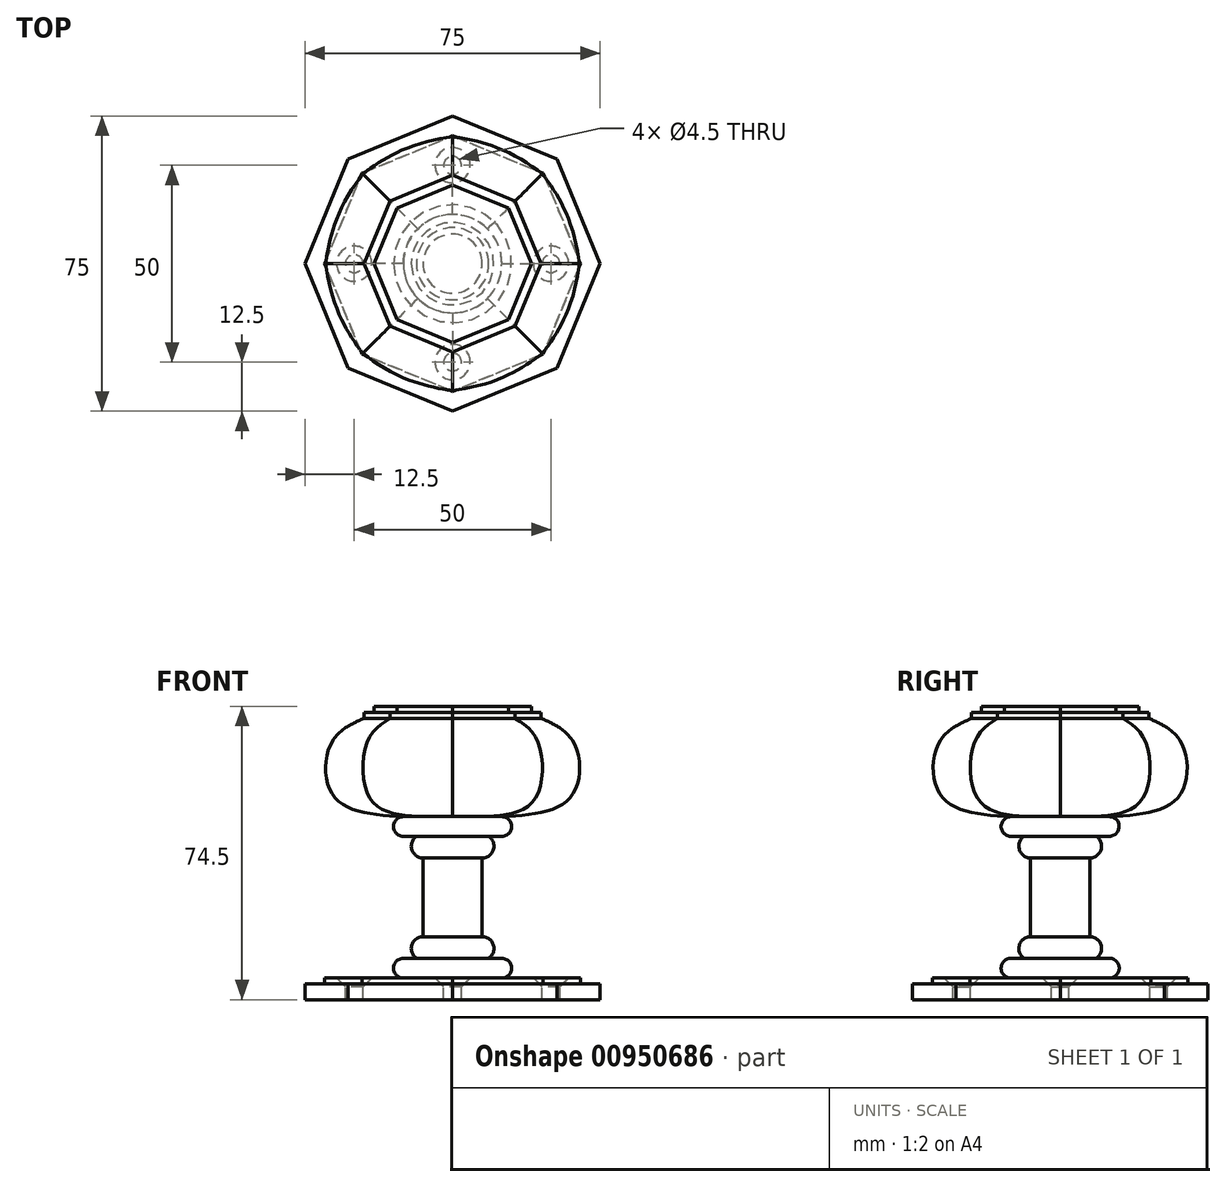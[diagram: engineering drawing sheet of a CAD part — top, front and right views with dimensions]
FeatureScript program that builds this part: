
annotation { "Feature Type Name" : "Feature", "Feature Type Description" : "" }
export const myFeature = defineFeature(function(context is Context, id is Id, definition is map)
    precondition{}
    {
        {
            var Q0;
            Q0=qCreatedBy(makeId("Top.planeOp"),FACE);
            var sketch = newSketch(context, id + "F0", { "sketchPlane" : qUnion([Q0])});
            skCircle(sketch, "E0.cCircle", {"center": v(0, 0) * mm, "radius": 37.5 * mm, "construction": true});
            skLineSegment(sketch, "E0.0", {"start": v(37.5, 0) * mm, "end": v(26.52, -26.52) * mm});
            skLineSegment(sketch, "E0.1", {"start": v(26.52, -26.52) * mm, "end": v(0, -37.5) * mm});
            skLineSegment(sketch, "E0.2", {"start": v(0, -37.5) * mm, "end": v(-26.52, -26.52) * mm});
            skLineSegment(sketch, "E0.3", {"start": v(-26.52, -26.52) * mm, "end": v(-37.5, 0) * mm});
            skLineSegment(sketch, "E0.4", {"start": v(-37.5, 0) * mm, "end": v(-26.52, 26.52) * mm});
            skLineSegment(sketch, "E0.5", {"start": v(-26.52, 26.52) * mm, "end": v(0, 37.5) * mm});
            skLineSegment(sketch, "E0.6", {"start": v(0, 37.5) * mm, "end": v(26.52, 26.52) * mm});
            skLineSegment(sketch, "E0.7", {"start": v(26.52, 26.52) * mm, "end": v(37.5, 0) * mm});
            skSolve(sketch);
        }
        {
            var Q0;
            Q0=makeQuery(id+"F0.imprint","IMPRINT",FACE,{"disambiguationData":[TD([[makeQuery(id+"F0.imprint","IMPRINT",EDGE,{"derivedFrom":sQuery(id+"F0.wireOp",EDGE,"E0.0")}),-1.0]])]});
            extrude(context, id + "F1", {"entities" : qUnion([Q0]), "depth" : 4 * mm, "offsetDistance" : 25 * mm});
        }
        {
            var Q0;
            Q0=makeQuery(id+"F1.opExtrude","CAP_FACE",FACE,{"disambiguationData":[OSD([sQuery(id+"F0.wireOp",EDGE,"E0.0"),sQuery(id+"F0.wireOp",EDGE,"E0.1"),sQuery(id+"F0.wireOp",EDGE,"E0.2"),sQuery(id+"F0.wireOp",EDGE,"E0.3"),sQuery(id+"F0.wireOp",EDGE,"E0.4"),sQuery(id+"F0.wireOp",EDGE,"E0.5"),sQuery(id+"F0.wireOp",EDGE,"E0.6"),sQuery(id+"F0.wireOp",EDGE,"E0.7")])],"isStart":false});
            var sketch = newSketch(context, id + "F2", { "sketchPlane" : qUnion([Q0])});
            skCircle(sketch, "E1.cCircle", {"center": v(0, 0) * mm, "radius": 32.5 * mm, "construction": true});
            skLineSegment(sketch, "E1.0", {"start": v(32.5, 0) * mm, "end": v(22.98, -22.98) * mm});
            skLineSegment(sketch, "E1.1", {"start": v(22.98, -22.98) * mm, "end": v(0, -32.5) * mm});
            skLineSegment(sketch, "E1.2", {"start": v(0, -32.5) * mm, "end": v(-22.98, -22.98) * mm});
            skLineSegment(sketch, "E1.3", {"start": v(-22.98, -22.98) * mm, "end": v(-32.5, 0) * mm});
            skLineSegment(sketch, "E1.4", {"start": v(-32.5, 0) * mm, "end": v(-22.98, 22.98) * mm});
            skLineSegment(sketch, "E1.5", {"start": v(-22.98, 22.98) * mm, "end": v(0, 32.5) * mm});
            skLineSegment(sketch, "E1.6", {"start": v(0, 32.5) * mm, "end": v(22.98, 22.98) * mm});
            skLineSegment(sketch, "E1.7", {"start": v(22.98, 22.98) * mm, "end": v(32.5, 0) * mm});
            skSolve(sketch);
        }
        {
            var Q0;
            Q0=makeQuery(id+"F2.imprint","IMPRINT",FACE,{"disambiguationData":[TD([[makeQuery(id+"F2.imprint","IMPRINT",EDGE,{"derivedFrom":sQuery(id+"F2.wireOp",EDGE,"E1.0")}),-1.0]])]});
            extrude(context, id + "F3", {"entities" : qUnion([Q0]), "operationType" : NewBodyOperationType.ADD, "depth" : 1.5 * mm, "offsetDistance" : 25 * mm});
        }
        {
            var Q0;
            Q0=qCreatedBy(makeId("Front.planeOp"),FACE);
            var sketch = newSketch(context, id + "F4", { "sketchPlane" : qUnion([Q0])});
            skLineSegment(sketch, "E2", {"start": v(0, 0) * mm, "end": v(0, 93.5) * mm, "construction": true});
            skLineSegment(sketch, "E3", {"start": v(7.5, 36) * mm, "end": v(7.5, 16) * mm});
            skLineSegment(sketch, "E4", {"start": v(12.5, 5.5) * mm, "end": v(0, 5.5) * mm});
            skLineSegment(sketch, "E5", {"start": v(7.5, 26) * mm, "end": v(0, 26) * mm, "construction": true});
            skLineSegment(sketch, "E6", {"start": v(0, 5.5) * mm, "end": v(0, 46.5) * mm});
            skLineSegment(sketch, "E7", {"start": v(9.16, 10.5) * mm, "end": v(12.5, 10.5) * mm});
            skArc(sketch, "E8", {"start": v(12.5, 5.5) * mm, "mid": v(15, 8) * mm, "end": v(12.5, 10.5) * mm});
            skArc(sketch, "E9", {"start": v(9.16, 10.5) * mm, "mid": v(10.37, 13.87) * mm, "end": v(7.5, 16) * mm});
            skArc(sketch, "E10.MirrorCS", {"start": v(9.16, 41.5) * mm, "mid": v(10.37, 38.13) * mm, "end": v(7.5, 36) * mm});
            skLineSegment(sketch, "E11.MirrorCS", {"start": v(9.16, 41.5) * mm, "end": v(12.5, 41.5) * mm});
            skArc(sketch, "E12.MirrorCS", {"start": v(12.5, 46.5) * mm, "mid": v(15, 44) * mm, "end": v(12.5, 41.5) * mm});
            skLineSegment(sketch, "E13", {"start": v(0, 46.5) * mm, "end": v(12.5, 46.5) * mm});
            skSolve(sketch);
        }
        {
            var Q0;
            Q0=makeQuery(id+"F4.imprint","IMPRINT",FACE,{"disambiguationData":[TD([[makeQuery(id+"F4.imprint","IMPRINT",EDGE,{"derivedFrom":sQuery(id+"F4.wireOp",EDGE,"E3")}),-1.0]])]});
            var Q1;
            Q1=sQuery(id+"F4.wireOp",EDGE,"E2");
            revolve(context, id + "F5", {"operationType" : NewBodyOperationType.ADD, "surfaceOperationType" : NewSurfaceOperationType.NEW, "entities" : qUnion([Q0]), "axis" : qUnion([Q1]), "revolveType" : RevolveType.FULL});
        }
        {
            var Q0;
            Q0=makeQuery(id+"F5.opRevolve","SWEPT_FACE",FACE,{"disambiguationData":[OSD([sQuery(id+"F4.wireOp",EDGE,"E13")])]});
            var sketch = newSketch(context, id + "F6", { "sketchPlane" : qUnion([Q0])});
            skCircle(sketch, "E14.0", {"center": v(0, 0) * mm, "radius": 12.5 * mm});
            skSolve(sketch);
        }
        {
            var Q0;
            Q0=makeQuery(id+"F5.opRevolve","SWEPT_FACE",FACE,{"disambiguationData":[OSD([sQuery(id+"F4.wireOp",EDGE,"E13")])]});
            cPlane(context, id + "F7", {"entities" : qUnion([Q0]), "cplaneType" : CPlaneType.OFFSET, "offset" : 5 * mm, "width" : 150 * mm, "height" : 150 * mm});
        }
        {
            var Q0;
            Q0=qCreatedBy(id+"F7.planeOp",FACE);
            var sketch = newSketch(context, id + "F8", { "sketchPlane" : qUnion([Q0])});
            skCircle(sketch, "E15.cCircle", {"center": v(0, 0) * mm, "radius": 30 * mm, "construction": true});
            skLineSegment(sketch, "E15.0", {"start": v(30, 0) * mm, "end": v(21.21, -21.21) * mm});
            skLineSegment(sketch, "E15.1", {"start": v(21.21, -21.21) * mm, "end": v(0, -30) * mm});
            skLineSegment(sketch, "E15.2", {"start": v(0, -30) * mm, "end": v(-21.21, -21.21) * mm});
            skLineSegment(sketch, "E15.3", {"start": v(-21.21, -21.21) * mm, "end": v(-30, 0) * mm});
            skLineSegment(sketch, "E15.4", {"start": v(-30, 0) * mm, "end": v(-21.21, 21.21) * mm});
            skLineSegment(sketch, "E15.5", {"start": v(-21.21, 21.21) * mm, "end": v(0, 30) * mm});
            skLineSegment(sketch, "E15.6", {"start": v(0, 30) * mm, "end": v(21.21, 21.21) * mm});
            skLineSegment(sketch, "E15.7", {"start": v(21.21, 21.21) * mm, "end": v(30, 0) * mm});
            skSolve(sketch);
        }
        {
            var Q0;
            Q0=qCreatedBy(id+"F7.planeOp",FACE);
            cPlane(context, id + "F9", {"entities" : qUnion([Q0]), "cplaneType" : CPlaneType.OFFSET, "offset" : 15 * mm, "width" : 150 * mm, "height" : 150 * mm});
        }
        {
            var Q0;
            Q0=qCreatedBy(id+"F9.planeOp",FACE);
            var sketch = newSketch(context, id + "F10", { "sketchPlane" : qUnion([Q0])});
            skCircle(sketch, "E16.0", {"center": v(0, 0) * mm, "radius": 30 * mm});
            skLineSegment(sketch, "E16.1", {"start": v(30, 0) * mm, "end": v(21.21, -21.21) * mm});
            skLineSegment(sketch, "E16.2", {"start": v(21.21, -21.21) * mm, "end": v(0, -30) * mm});
            skLineSegment(sketch, "E16.3", {"start": v(0, -30) * mm, "end": v(-21.21, -21.21) * mm});
            skLineSegment(sketch, "E16.4", {"start": v(-21.21, -21.21) * mm, "end": v(-30, 0) * mm});
            skLineSegment(sketch, "E16.5", {"start": v(-30, 0) * mm, "end": v(-21.21, 21.21) * mm});
            skLineSegment(sketch, "E16.6", {"start": v(-21.21, 21.21) * mm, "end": v(0, 30) * mm});
            skLineSegment(sketch, "E16.7", {"start": v(0, 30) * mm, "end": v(21.21, 21.21) * mm});
            skLineSegment(sketch, "E16.8", {"start": v(21.21, 21.21) * mm, "end": v(30, 0) * mm});
            skSolve(sketch);
        }
        {
            var Q0;
            Q0=qCreatedBy(id+"F9.planeOp",FACE);
            cPlane(context, id + "F11", {"entities" : qUnion([Q0]), "cplaneType" : CPlaneType.OFFSET, "offset" : 5 * mm, "width" : 150 * mm, "height" : 150 * mm});
        }
        {
            var Q0;
            Q0=qCreatedBy(id+"F11.planeOp",FACE);
            var sketch = newSketch(context, id + "F12", { "sketchPlane" : qUnion([Q0])});
            skCircle(sketch, "E17.cCircle", {"center": v(0, 0) * mm, "radius": 22.5 * mm, "construction": true});
            skLineSegment(sketch, "E17.0", {"start": v(22.5, 0) * mm, "end": v(15.9, -15.9) * mm});
            skLineSegment(sketch, "E17.1", {"start": v(15.9, -15.9) * mm, "end": v(0, -22.5) * mm});
            skLineSegment(sketch, "E17.2", {"start": v(0, -22.5) * mm, "end": v(-15.9, -15.9) * mm});
            skLineSegment(sketch, "E17.3", {"start": v(-15.9, -15.9) * mm, "end": v(-22.5, 0) * mm});
            skLineSegment(sketch, "E17.4", {"start": v(-22.5, 0) * mm, "end": v(-15.9, 15.9) * mm});
            skLineSegment(sketch, "E17.5", {"start": v(-15.9, 15.9) * mm, "end": v(0, 22.5) * mm});
            skLineSegment(sketch, "E17.6", {"start": v(0, 22.5) * mm, "end": v(15.9, 15.9) * mm});
            skLineSegment(sketch, "E17.7", {"start": v(15.9, 15.9) * mm, "end": v(22.5, 0) * mm});
            skSolve(sketch);
        }
        {
            var Q1;
            Q1=qSketchRegion(id+"F6",true);
            var Q2;
            Q2=qSketchRegion(id+"F8",true);
            var Q3;
            Q3=qSketchRegion(id+"F10",true);
            var Q4;
            Q4=qSketchRegion(id+"F12",true);
            loft(context, id + "F13", {"operationType" : NewBodyOperationType.ADD, "sheetProfilesArray" : [{ "sheetProfileEntities" : qUnion([Q1]) }, { "sheetProfileEntities" : qUnion([Q2]) }, { "sheetProfileEntities" : qUnion([Q3]) }, { "sheetProfileEntities" : qUnion([Q4]) }]});
        }
        {
            var Q0;
            Q0=makeQuery(id+"F13.opLoft","CAP_FACE",FACE,{"disambiguationData":[OSD([makeQuery(id+"F12.imprint","IMPRINT",FACE,{"disambiguationData":[TD([[makeQuery(id+"F12.imprint","IMPRINT",EDGE,{"derivedFrom":sQuery(id+"F12.wireOp",EDGE,"E17.0")}),-1.0]])]})])],"isStart":true});
            extrude(context, id + "F14", {"entities" : qUnion([Q0]), "operationType" : NewBodyOperationType.ADD, "depth" : 1.5 * mm, "offsetDistance" : 25 * mm});
        }
        {
            var Q0;
            Q0=makeQuery(id+"F14.opExtrude","CAP_FACE",FACE,{"disambiguationData":[OSD([makeQuery(id+"F12.imprint","IMPRINT",FACE,{"disambiguationData":[TD([[makeQuery(id+"F12.imprint","IMPRINT",EDGE,{"derivedFrom":sQuery(id+"F12.wireOp",EDGE,"E17.0")}),-1.0]])]})])],"isStart":false});
            var sketch = newSketch(context, id + "F15", { "sketchPlane" : qUnion([Q0])});
            skCircle(sketch, "E18.cCircle", {"center": v(0, 0) * mm, "radius": 20 * mm, "construction": true});
            skLineSegment(sketch, "E18.0", {"start": v(20, 0) * mm, "end": v(14.14, -14.14) * mm});
            skLineSegment(sketch, "E18.1", {"start": v(14.14, -14.14) * mm, "end": v(0, -20) * mm});
            skLineSegment(sketch, "E18.2", {"start": v(0, -20) * mm, "end": v(-14.14, -14.14) * mm});
            skLineSegment(sketch, "E18.3", {"start": v(-14.14, -14.14) * mm, "end": v(-20, 0) * mm});
            skLineSegment(sketch, "E18.4", {"start": v(-20, 0) * mm, "end": v(-14.14, 14.14) * mm});
            skLineSegment(sketch, "E18.5", {"start": v(-14.14, 14.14) * mm, "end": v(0, 20) * mm});
            skLineSegment(sketch, "E18.6", {"start": v(0, 20) * mm, "end": v(14.14, 14.14) * mm});
            skLineSegment(sketch, "E18.7", {"start": v(14.14, 14.14) * mm, "end": v(20, 0) * mm});
            skSolve(sketch);
        }
        {
            var Q0;
            Q0=makeQuery(id+"F15.imprint","IMPRINT",FACE,{"disambiguationData":[TD([[makeQuery(id+"F15.imprint","IMPRINT",EDGE,{"derivedFrom":sQuery(id+"F15.wireOp",EDGE,"E18.0")}),-1.0]])]});
            extrude(context, id + "F16", {"entities" : qUnion([Q0]), "operationType" : NewBodyOperationType.ADD, "depth" : 1.5 * mm, "offsetDistance" : 25 * mm});
        }
        {
            var Q0;
            Q0=makeQuery(id+"F3.opExtrude","CAP_FACE",FACE,{"disambiguationData":[OSD([sQuery(id+"F2.wireOp",EDGE,"E1.0"),sQuery(id+"F2.wireOp",EDGE,"E1.1"),sQuery(id+"F2.wireOp",EDGE,"E1.2"),sQuery(id+"F2.wireOp",EDGE,"E1.3"),sQuery(id+"F2.wireOp",EDGE,"E1.4"),sQuery(id+"F2.wireOp",EDGE,"E1.5"),sQuery(id+"F2.wireOp",EDGE,"E1.6"),sQuery(id+"F2.wireOp",EDGE,"E1.7")])],"isStart":false});
            var sketch = newSketch(context, id + "F17", { "sketchPlane" : qUnion([Q0])});
            skPoint(sketch, "E19", {"position": v(-25, 0) * mm});
            skCircle(sketch, "E20", {"center": v(0, 0) * mm, "radius": 25 * mm, "construction": true});
            skPoint(sketch, "E21", {"position": v(25, 0) * mm});
            skPoint(sketch, "E22", {"position": v(0, 25) * mm});
            skPoint(sketch, "E23", {"position": v(0, -25) * mm});
            skSolve(sketch);
        }
        {
            var Q0;
            Q0=sQuery(id+"F17.wireOp",VERTEX,"E19");
            var Q1;
            Q1=sQuery(id+"F17.wireOp",VERTEX,"E23");
            var Q2;
            Q2=sQuery(id+"F17.wireOp",VERTEX,"E21");
            var Q3;
            Q3=sQuery(id+"F17.wireOp",VERTEX,"E22");
            var Q4;
            Q4=makeQuery(id+"F1.opExtrude","SWEPT_BODY",BODY,{"disambiguationData":[OSD([sQuery(id+"F0.wireOp",EDGE,"E0.0"),sQuery(id+"F0.wireOp",EDGE,"E0.1"),sQuery(id+"F0.wireOp",EDGE,"E0.2"),sQuery(id+"F0.wireOp",EDGE,"E0.3"),sQuery(id+"F0.wireOp",EDGE,"E0.4"),sQuery(id+"F0.wireOp",EDGE,"E0.5"),sQuery(id+"F0.wireOp",EDGE,"E0.6"),sQuery(id+"F0.wireOp",EDGE,"E0.7")])]});
            hole(context, id + "F18", {"style" : HoleStyle.C_SINK, "endStyle" : HoleEndStyle.BLIND, "standardTappedOrClearance" : lookupTablePath({ "fit" : "Normal", "standard" : "ISO", "size" : "M4", "type" : "Clearance" }), "standardBlindInLast" : lookupTablePath({ "fit" : "Normal", "standard" : "ISO", "engagement" : "75%", "pitch" : "0.7 mm", "size" : "M4", "type" : "Clearance & tapped" }), "holeDiameter" : 4.5 * mm, "cSinkDiameter" : 8.96 * mm, "cSinkAngle" : 90 * degree, "majorDiameter" : 4 * mm, "holeDepth" : 8 * mm, "isTappedThrough" : true, "tappedDepth" : 5.9 * mm, "tapClearance" : 3, "locations" : qUnion([Q0, Q1, Q2, Q3]), "scope" : qUnion([Q4])});
        }
    });
